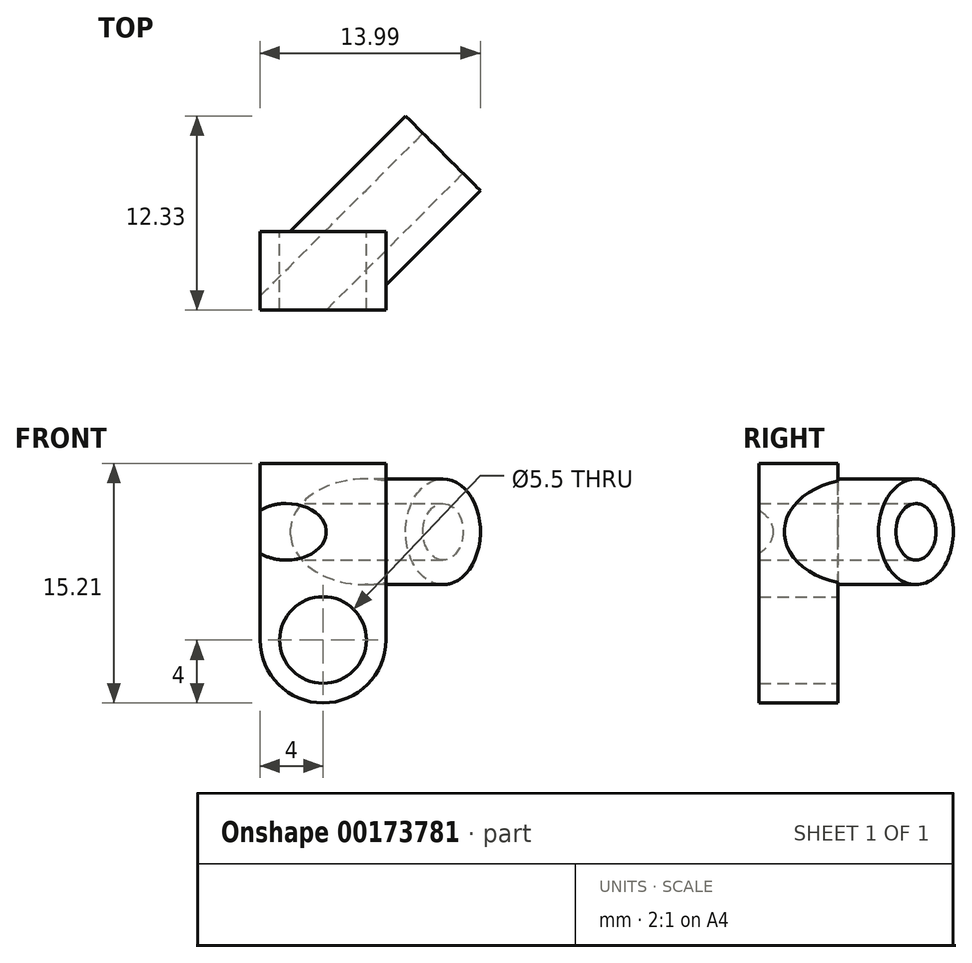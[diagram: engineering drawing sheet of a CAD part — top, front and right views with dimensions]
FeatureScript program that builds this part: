
annotation { "Feature Type Name" : "Feature", "Feature Type Description" : "" }
export const myFeature = defineFeature(function(context is Context, id is Id, definition is map)
    precondition{}
    {
        {
            var Q0;
            Q0=qCreatedBy(makeId("Front.planeOp"),FACE);
            var sketch = newSketch(context, id + "F0", { "sketchPlane" : qUnion([Q0])});
            skCircle(sketch, "E0", {"center": v(0, 0) * mm, "radius": 2.75 * mm});
            skCircle(sketch, "E1", {"center": v(0, 0) * mm, "radius": 4 * mm});
            skLineSegment(sketch, "E2", {"start": v(-4, 0) * mm, "end": v(0, 0) * mm});
            skLineSegment(sketch, "E3", {"start": v(0, 0) * mm, "end": v(4, 0) * mm});
            skLineSegment(sketch, "E4.bottom", {"start": v(-4, 0) * mm, "end": v(4, 0) * mm});
            skLineSegment(sketch, "E4.top", {"start": v(-4, 11.2) * mm, "end": v(4, 11.2) * mm});
            skLineSegment(sketch, "E4.left", {"start": v(-4, 0) * mm, "end": v(-4, 11.2) * mm});
            skLineSegment(sketch, "E4.right", {"start": v(4, 0) * mm, "end": v(4, 11.2) * mm});
            skCircle(sketch, "E5", {"center": v(-17.9, 0) * mm, "radius": 2.75 * mm});
            skCircle(sketch, "E6", {"center": v(-17.9, 0) * mm, "radius": 4 * mm});
            skLineSegment(sketch, "E7.bottom", {"start": v(-21.9, 0) * mm, "end": v(-13.9, 0) * mm});
            skLineSegment(sketch, "E7.left", {"start": v(-21.9, 0) * mm, "end": v(-21.9, 11.2) * mm});
            skLineSegment(sketch, "E7.right", {"start": v(-13.9, 0) * mm, "end": v(-13.9, 11.2) * mm});
            skLineSegment(sketch, "E8", {"start": v(-13.9, 11.2) * mm, "end": v(-21.9, 11.2) * mm});
            skSolve(sketch);
        }
        {
            var Q0;
            Q0=makeQuery(id+"F0.imprint","IMPRINT",FACE,{"disambiguationData":[TD([[makeQuery(id+"F0.imprint","IMPRINT",EDGE,{"derivedFrom":sQuery(id+"F0.wireOp",EDGE,"E4.top")}),-1.0]])]});
            var Q1;
            {var subQ0=sQuery(id+"F0.wireOp",EDGE,"E4.bottom");var subQ1=sQuery(id+"F0.wireOp",EDGE,"E0");var subQ2=makeQuery(id+"F0.imprint","INTERSECT",VERTEX,{"disambiguationData":[OD(0.0)],"derivedFrom":[subQ1,subQ0]});Q1=makeQuery(id+"F0.imprint","IMPRINT",FACE,{"disambiguationData":[TD([[makeQuery(id+"F0.imprint","IMPRINT",EDGE,{"disambiguationData":[TD([[subQ2,1.0]])],"derivedFrom":subQ1}),-1.0]])]});}
            var Q2;
            {var subQ0=sQuery(id+"F0.wireOp",EDGE,"E4.bottom");var subQ1=sQuery(id+"F0.wireOp",EDGE,"E0");var subQ2=makeQuery(id+"F0.imprint","INTERSECT",VERTEX,{"disambiguationData":[OD(0.0)],"derivedFrom":[subQ1,subQ0]});Q2=makeQuery(id+"F0.imprint","IMPRINT",FACE,{"disambiguationData":[TD([[makeQuery(id+"F0.imprint","IMPRINT",EDGE,{"disambiguationData":[TD([[subQ2,-1.0]])],"derivedFrom":subQ1}),-1.0]])]});}
            extrude(context, id + "F1", {"entities" : qUnion([Q0, Q1, Q2]), "depth" : 5 * mm, "offsetDistance" : 25 * mm});
        }
        {
            var Q0;
            Q0=makeQuery(id+"F1.opExtrude","CAP_EDGE",EDGE,{"disambiguationData":[OSD([sQuery(id+"F0.wireOp",EDGE,"E4.right")])],"isStart":false});
            cPlane(context, id + "F2", {"entities" : qUnion([Q0]), "cplaneType" : CPlaneType.LINE_ANGLE, "offset" : 25 * mm, "angle" : 45 * degree, "width" : 150 * mm, "height" : 150 * mm});
        }
        {
            var Q0;
            Q0=qCreatedBy(id+"F2.planeOp",FACE);
            cPlane(context, id + "F3", {"entities" : qUnion([Q0]), "cplaneType" : CPlaneType.OFFSET, "offset" : 4.6 * mm, "width" : 150 * mm, "height" : 150 * mm});
        }
        {
            var Q0;
            Q0=qCreatedBy(id+"F3.planeOp",FACE);
            var sketch = newSketch(context, id + "F4", { "sketchPlane" : qUnion([Q0])});
            skCircle(sketch, "E9", {"center": v(-1.88, 6.87) * mm, "radius": 1.8 * mm});
            skCircle(sketch, "E10", {"center": v(-1.88, 6.87) * mm, "radius": 3.36 * mm});
            skSolve(sketch);
        }
        {
            var Q0;
            Q0=makeQuery(id+"F4.imprint","IMPRINT",FACE,{"disambiguationData":[TD([[makeQuery(id+"F4.imprint","IMPRINT",EDGE,{"derivedFrom":sQuery(id+"F4.wireOp",EDGE,"E9")}),1.0]])]});
            extrude(context, id + "F5", {"entities" : qUnion([Q0]), "operationType" : NewBodyOperationType.REMOVE, "oppositeDirection" : true, "depth" : 25 * mm, "offsetDistance" : 25 * mm});
        }
        {
            var Q0;
            Q0=makeQuery(id+"F4.imprint","IMPRINT",FACE,{"disambiguationData":[TD([[makeQuery(id+"F4.imprint","IMPRINT",EDGE,{"derivedFrom":sQuery(id+"F4.wireOp",EDGE,"E9")}),-1.0]])]});
            extrude(context, id + "F6", {"entities" : qUnion([Q0]), "operationType" : NewBodyOperationType.ADD, "depth" : 5 * mm, "offsetDistance" : 25 * mm, "hasSecondDirection" : true, "secondDirectionOppositeDirection" : true, "secondDirectionDepth" : 5.36 * mm});
        }
    });
